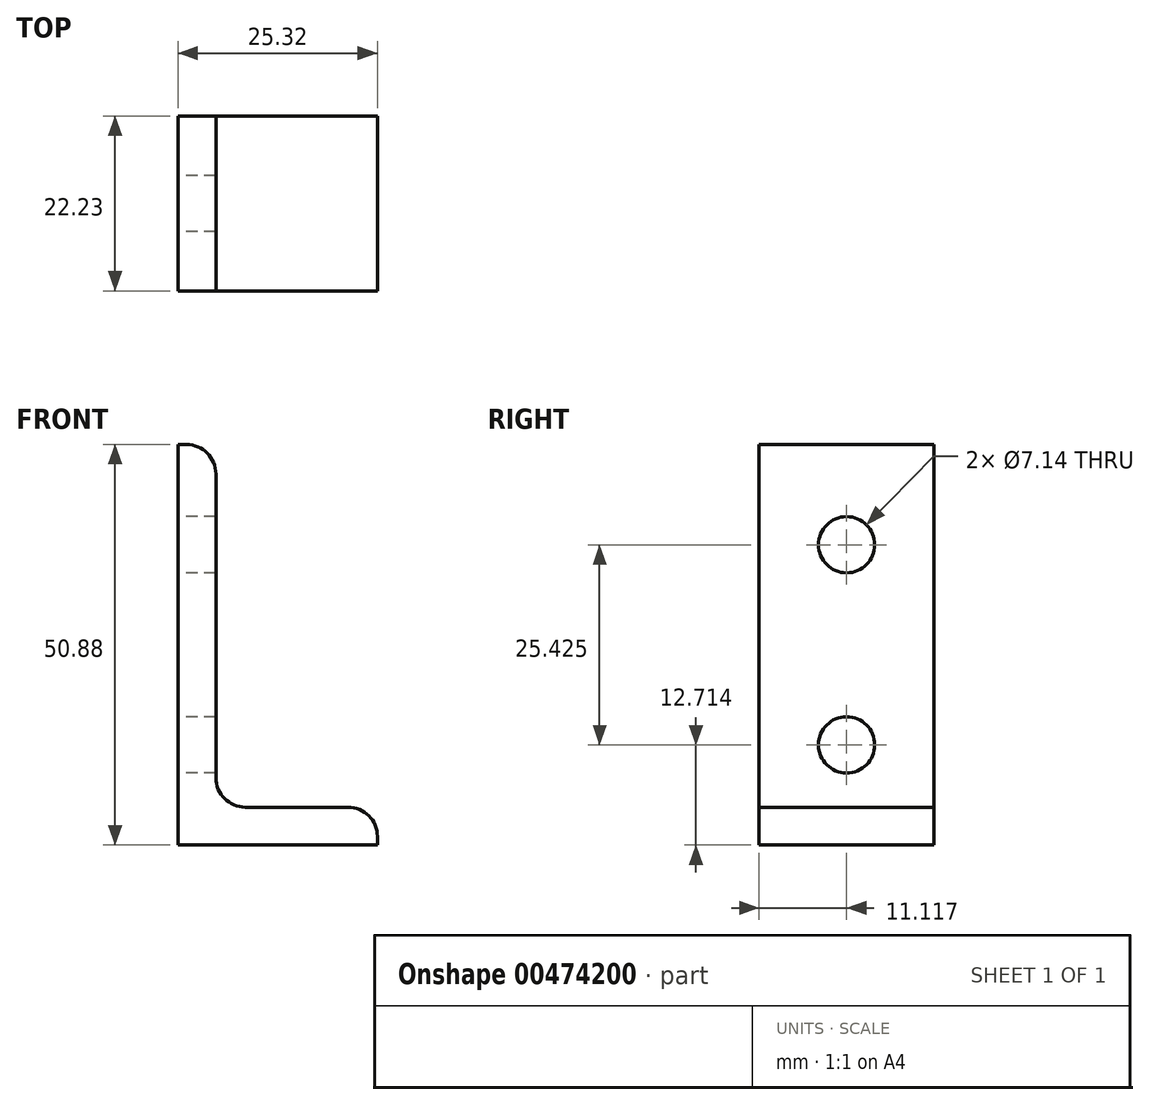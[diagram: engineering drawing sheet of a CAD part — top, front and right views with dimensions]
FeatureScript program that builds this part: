
annotation { "Feature Type Name" : "Feature", "Feature Type Description" : "" }
export const myFeature = defineFeature(function(context is Context, id is Id, definition is map)
    precondition{}
    {
        {
            var Q0;
            Q0=qCreatedBy(makeId("Front.planeOp"),FACE);
            var sketch = newSketch(context, id + "F0", { "sketchPlane" : qUnion([Q0])});
            skLineSegment(sketch, "E0", {"start": v(0, 34.43) * mm, "end": v(0, -16.45) * mm});
            skLineSegment(sketch, "E1", {"start": v(0, -16.45) * mm, "end": v(25.32, -16.45) * mm});
            skLineSegment(sketch, "E2", {"start": v(25.32, -16.45) * mm, "end": v(25.32, -11.65) * mm});
            skLineSegment(sketch, "E3", {"start": v(25.32, -11.65) * mm, "end": v(4.8, -11.65) * mm});
            skLineSegment(sketch, "E4", {"start": v(4.8, -11.65) * mm, "end": v(4.8, 34.43) * mm});
            skLineSegment(sketch, "E5", {"start": v(4.8, 34.43) * mm, "end": v(0, 34.43) * mm});
            skSolve(sketch);
        }
        {
            var Q0;
            Q0 = qSketchRegion(id + "F0", true);
            extrude(context, id + "F1", {"entities" : qUnion([Q0]), "depth" : 22.22 * mm, "offsetDistance" : 25.4 * mm});
        }
        {
            var Q0;
            Q0=makeQuery(id+"F1.opExtrude","SWEPT_EDGE",EDGE,{"disambiguationData":[OSD([sQuery(id+"F0.wireOp",EDGE,"E4"),sQuery(id+"F0.wireOp",EDGE,"E5")])]});
            var Q1;
            Q1=makeQuery(id+"F1.opExtrude","SWEPT_EDGE",EDGE,{"disambiguationData":[OSD([sQuery(id+"F0.wireOp",EDGE,"E3"),sQuery(id+"F0.wireOp",EDGE,"E4")])]});
            var Q2;
            Q2=makeQuery(id+"F1.opExtrude","SWEPT_EDGE",EDGE,{"disambiguationData":[OSD([sQuery(id+"F0.wireOp",EDGE,"E2"),sQuery(id+"F0.wireOp",EDGE,"E3")])]});
            fillet(context, id + "F2", {"entities" : qUnion([Q0, Q1, Q2]), "radius" : 3.74 * mm, "tangentPropagation" : true, "allowEdgeOverflow" : false});
        }
        {
            var Q0;
            Q0=makeQuery(id+"F1.opExtrude","SWEPT_FACE",FACE,{"disambiguationData":[OSD([sQuery(id+"F0.wireOp",EDGE,"E0")])]});
            var sketch = newSketch(context, id + "F3", { "sketchPlane" : qUnion([Q0])});
            skCircle(sketch, "E6", {"center": v(11.11, 21.69) * mm, "radius": 3.57 * mm});
            skPoint(sketch, "E6.centerSnap0", {"position": v(11.11, 34.43) * mm});
            skCircle(sketch, "E7", {"center": v(11.11, -3.74) * mm, "radius": 3.57 * mm});
            skSolve(sketch);
        }
        {
            var Q0;
            Q0=makeQuery(id+"F3.imprint","IMPRINT",FACE,{"disambiguationData":[TD([[makeQuery(id+"F3.imprint","IMPRINT",EDGE,{"derivedFrom":sQuery(id+"F3.wireOp",EDGE,"E6")}),1.0]])]});
            var Q1;
            Q1=makeQuery(id+"F3.imprint","IMPRINT",FACE,{"disambiguationData":[TD([[makeQuery(id+"F3.imprint","IMPRINT",EDGE,{"derivedFrom":sQuery(id+"F3.wireOp",EDGE,"E7")}),1.0]])]});
            extrude(context, id + "F4", {"entities" : qUnion([Q0, Q1]), "operationType" : NewBodyOperationType.REMOVE, "oppositeDirection" : true, "depth" : 4.8 * mm, "offsetDistance" : 25.4 * mm});
        }
    });
